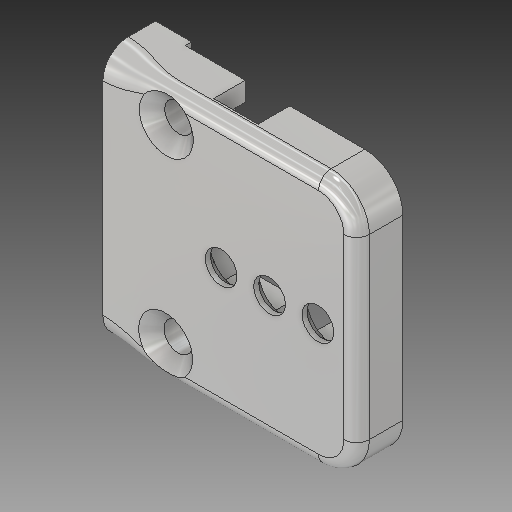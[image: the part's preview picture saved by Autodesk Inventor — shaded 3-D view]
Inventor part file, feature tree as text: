
AUTODESK INVENTOR PART (.ipt)
format: ipt  version: 2018 (Build 220112000, 112)  size: 413,184 bytes
history: native  units: mm
features: reference x24, extrude x7, sketch x6, projected_geometry x4, other x4, plane x3, chamfer x2, fillet x1
ambient origin geometry x8: Origin, YZ Plane, XZ Plane, XY Plane, X Axis, Y Axis, Z Axis, Center Point
bodies: Solid1 (feature_tree)
feature tree (51):
  sketch  "Sketch1"  dims[d0=4.5mm d1=7.3mm d2=0.0mm]
  plane  "Work Plane1"
  extrude  "Extrusion1"  Depth=7.3mm TaperAngle=0.0deg
  sketch  "Sketch2"  dims[d3=40.0mm d4=0.3mm]
  plane  "Work Plane2"
  plane  "Work Plane3"
  extrude  "Extrusion2"  Depth=0.3mm
  extrude  "Extrusion3"  Depth=10.0mm
  extrude  "Extrusion4"  Depth=8.0mm
  extrude  "Extrusion5"  Depth=8.0mm
  extrude  "Extrusion6"  Depth=11.0mm
  extrude  "Extrusion7"  Depth=11.0mm
  fillet  "Fillet1"  Radius=6.8mm
  chamfer  "Chamfer1"  Distance=5.0mm
  chamfer  "Chamfer2"  Distance=1.0mm
  reference  "Reference1"
  reference  "Reference2"
  reference  "Reference3"
  reference  "Reference4"
  reference  "Reference5"
  reference  "Reference6"
  reference  "Reference7"
  reference  "Reference8"
  reference  "Reference9"
  reference  "Reference10"
  reference  "Reference11"
  sketch  "Sketch3"  dims[d5=10.0mm d6=0.0mm d7=8.0mm]
  reference  "Reference12"
  reference  "Reference13"
  projected_geometry  "Projected Loop1"
  projected_geometry  "Projected Loop2"
  projected_geometry  "Projected Loop3"
  sketch  "Sketch5"  dims[d8=5.0mm d9=8.0mm]
  projected_geometry  "Projected Loop4"
  sketch  "Sketch6"  dims[d10=5.0mm d11=8.0mm]
  reference  "Reference14"
  reference  "Reference15"
  reference  "Reference16"
  reference  "Reference17"
  reference  "Reference18"
  reference  "Reference19"
  reference  "Reference20"
  reference  "Reference21"
  sketch  "Sketch7"  dims[d12=5.0mm d13=11.0mm d14=11.0mm d15=6.8mm d16=0.0mm d19=5.0mm d20=1.0mm d21=8.0mm d22=5.0mm d23=6.0mm d24=0.0mm d25=0.5mm d26=0.5mm d27=0.5mm d28=0.5mm d29=5.0mm d30=0.0mm d31=0.5mm d32=0.5mm d33=1.5mm d34=1.5mm d35=5.0mm d36=0.0mm d37=5.0mm d38=5.0mm d39=0.0mm d40=4.0mm d41=4.0mm d42=2.0mm d43=6.459mm d44=2.0mm d45=3.547mm d46=2.0mm d47=2.0mm d48=45.0deg d49=1.5mm d50=2.0mm d51=45.0deg d53=3.0mm d55=3.0mm d57=1.0mm d58=1.0mm d59=22.065003mm]
  reference  "Reference22"
  reference  "Reference23"
  reference  "Reference24"
  other  "<userpath>\Dropbox\Skola\Projekt\Kretsn_Brillz_V2\3D\Main.iam"
  other  "Main.iam"
  other  "Holster_Bottom:1"
  other  "SchematicBKP_Shrinkwrap_1:1"
